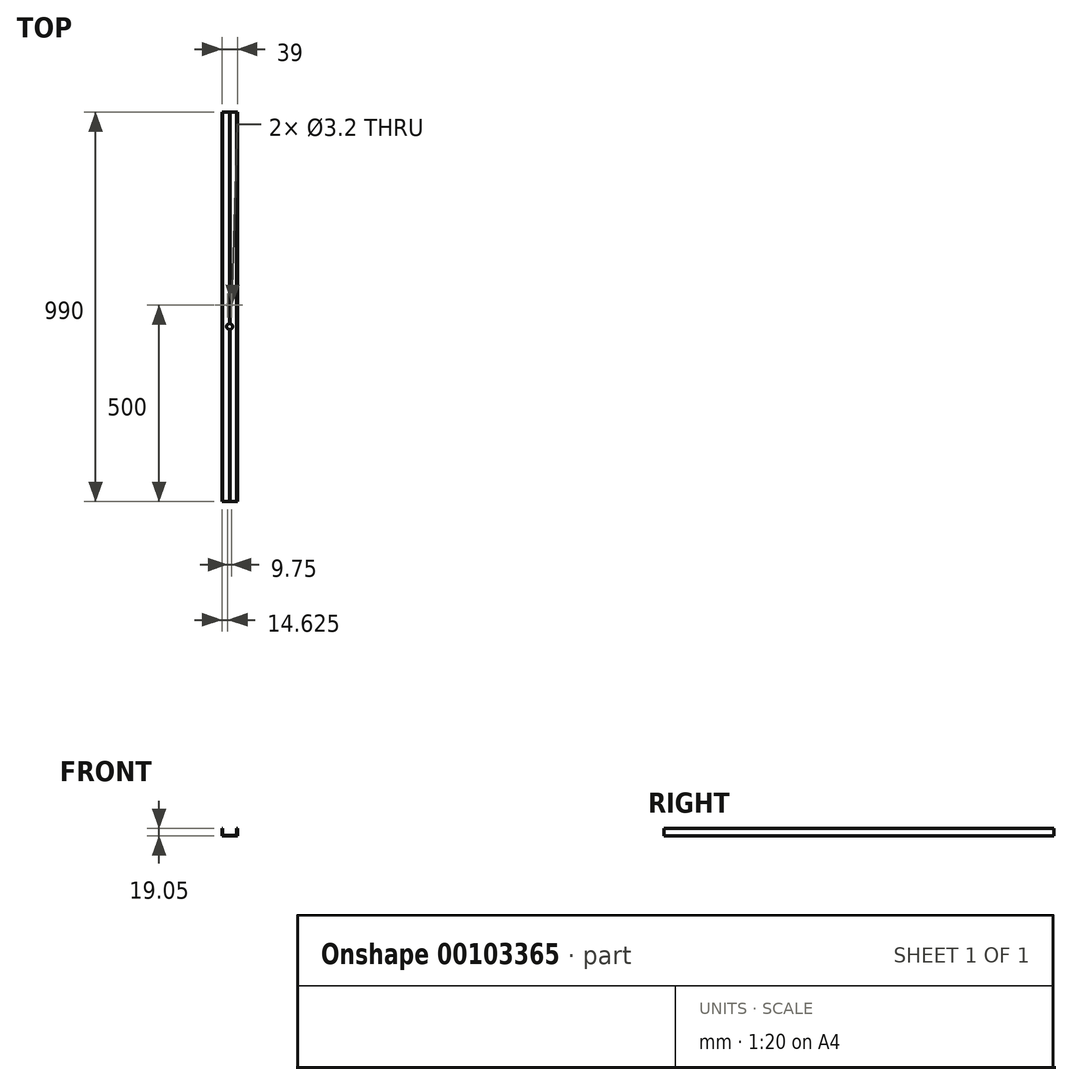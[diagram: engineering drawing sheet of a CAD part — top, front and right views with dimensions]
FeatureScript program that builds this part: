
annotation { "Feature Type Name" : "Feature", "Feature Type Description" : "" }
export const myFeature = defineFeature(function(context is Context, id is Id, definition is map)
    precondition{}
    {
        {
            var Q0;
            Q0=qCreatedBy(makeId("Front.planeOp"),FACE);
            var sketch = newSketch(context, id + "F0", { "sketchPlane" : qUnion([Q0])});
            skLineSegment(sketch, "E0", {"start": v(-19.5, 0) * mm, "end": v(-19.5, 19.05) * mm});
            skLineSegment(sketch, "E1", {"start": v(-18, 19.05) * mm, "end": v(-18, 1.5) * mm});
            skLineSegment(sketch, "E2", {"start": v(-0.45, 1.5) * mm, "end": v(-18, 1.5) * mm});
            skLineSegment(sketch, "E3", {"start": v(-0.45, 1.5) * mm, "end": v(-0.45, 0) * mm});
            skLineSegment(sketch, "E4", {"start": v(-19.5, 0) * mm, "end": v(-0.45, 0) * mm});
            skLineSegment(sketch, "E5", {"start": v(-19.5, 19.05) * mm, "end": v(-18, 19.05) * mm});
            skLineSegment(sketch, "E6", {"start": v(0, 0) * mm, "end": v(0, 19.05) * mm, "construction": true});
            skLineSegment(sketch, "E7.MirrorCS", {"start": v(19.5, 0) * mm, "end": v(19.5, 19.05) * mm});
            skLineSegment(sketch, "E8.MirrorCS", {"start": v(19.5, 19.05) * mm, "end": v(18, 19.05) * mm});
            skLineSegment(sketch, "E9.MirrorCS", {"start": v(18, 19.05) * mm, "end": v(18, 1.5) * mm});
            skLineSegment(sketch, "E10.MirrorCS", {"start": v(0.45, 1.5) * mm, "end": v(18, 1.5) * mm});
            skLineSegment(sketch, "E11.MirrorCS", {"start": v(0.45, 1.5) * mm, "end": v(0.45, 0) * mm});
            skLineSegment(sketch, "E12.MirrorCS", {"start": v(19.5, 0) * mm, "end": v(0.45, 0) * mm});
            skSolve(sketch);
        }
        {
            var Q0;
            Q0=qSketchRegion(id+"F0",true);
            extrude(context, id + "F1", {"entities" : qUnion([Q0]), "endBound" : BoundingType.SYMMETRIC, "depth" : (1000 - 5 * 2) * mm});
        }
        {
            var Q0;
            Q0=makeQuery(id+"F1.opExtrude","SWEPT_FACE",FACE,{"disambiguationData":[OSD([sQuery(id+"F0.wireOp",EDGE,"E2")])]});
            var sketch = newSketch(context, id + "F2", { "sketchPlane" : qUnion([Q0])});
            skLineSegment(sketch, "E13", {"start": v(0, 5) * mm, "end": v(-4.88, 5) * mm, "construction": true});
            skLineSegment(sketch, "E14", {"start": v(0, 5) * mm, "end": v(4.87, 5) * mm, "construction": true});
            skCircle(sketch, "E15", {"center": v(-4.88, 5) * mm, "radius": 1.6 * mm});
            skCircle(sketch, "E16", {"center": v(4.87, 5) * mm, "radius": 1.6 * mm});
            skLineSegment(sketch, "E17", {"start": v(0, 0) * mm, "end": v(0, 5) * mm, "construction": true});
            skSolve(sketch);
        }
        {
            var Q0;
            Q0=qSketchRegion(id+"F2",true);
            extrude(context, id + "F3", {"entities" : qUnion([Q0]), "operationType" : NewBodyOperationType.REMOVE, "endBound" : BoundingType.THROUGH_ALL, "oppositeDirection" : true, "depth" : 25 * mm});
        }
        {
            var Q0;
            Q0=makeQuery(id+"F1.opExtrude","SWEPT_FACE",FACE,{"disambiguationData":[OSD([sQuery(id+"F0.wireOp",EDGE,"E2")])]});
            var sketch = newSketch(context, id + "F4", { "sketchPlane" : qUnion([Q0])});
            skLineSegment(sketch, "E18", {"start": v(0, 0) * mm, "end": v(0, -50) * mm, "construction": true});
            skCircle(sketch, "E19", {"center": v(0, -50) * mm, "radius": 7.5 * mm});
            skSolve(sketch);
        }
        {
            var Q0;
            Q0=qSketchRegion(id+"F4",true);
            extrude(context, id + "F5", {"entities" : qUnion([Q0]), "operationType" : NewBodyOperationType.REMOVE, "endBound" : BoundingType.THROUGH_ALL, "oppositeDirection" : true, "depth" : 25 * mm});
        }
    });
